# Revit family: Haworth_Enclose_Wall_Solid_Special
name_source: partatom
category: Furniture Systems
revit_build: Autodesk Revit 2018 (Build: 20170223_1515(x64)
units: mm (PartAtom-declared; Revit-internal decimal feet)

## family parameters
Always vertical = Yes
Cut with Voids When Loaded = No
OmniClass Number = 23.25.40.14
OmniClass Title = Demountable Partitions
Part Type = Normal
Room Calculation Point = No
Round Connector Dimension = Use Diameter
Shared = Yes
Work Plane-Based = No

## types (1)
- 36" x 40"
    # of Panels Back = 1
    # of Panels Front = 1
    Actual # of Panels Back = 1
    Actual # of Panels Front = 1
    Actual Height = 40 "
    Actual Panel 1 Back Height = 32 "
    Actual Panel 1 Front Height = 32 "
    Actual Panel 2 Back Height = 32 "
    Actual Panel 2 Front Height = 32 "
    Actual Width = 36 "
    Assembly Code = C1010200
    Base Height = 1.25 "
    Cap Height = 1 "
    Ceiling Mount = Yes
    Description = Wall Solid - Special
    End of Run Finish = Haworth _ Polymer _ Black
    End of Run Width = 0.155 "
    Frame Depth = 4 "
    Frame Finish = Haworth _ Metal _ Brushed Aluminum
    Glass Offset = 4.75 "
    Height = 40 "
    Horizontal Bottom Adjuster Width = 3.875 "
    Horizontal Bottom Trim Width = 2.5 "
    Horizontal Frame Width = 0.875 "
    Horizontal Top Adjuster Width = 2.625 "
    Horizontal Top Trim Width = 1.5 "
    Manufacturer = Haworth
    Material Options = http://surfaces.haworth.com
    Max # of Panels = 3
    Max. Height = 144 "
    Max. Width = 60 "
    Min. Height = 24 "
    Min. Width = 8 "
    Min/Max Height = 84-144 in.
    Min/Max Width = 8-60 in.
    Model = Haworth - Enclose
    Offset Back = 9.84 "
    Offset Front = 9.84 "
    Panel 1 Back Height = 32 "
    Panel 1 Front Height = 32 "
    Panel 2 Back Height = 64 "
    Panel 2 Front Height = 64 "
    Panel Depth = 0.5 "
    Panel Height Back = 29.16 "
    Panel Height Front = 29.16 "
    Panel Height Note = All Heights are A.F.F.
    Panel Size Note = 8in increments
    Panel Width = 35.69 "
    Raceway Finish = Haworth _ Metal _ Brushed Aluminum
    Raceway Panel Back = Yes
    Raceway Panel Back Height = 8.59 "
    Raceway Panel Front = Yes
    Raceway Panel Front Height = 8.59 "
    Raceway Panel Width = 35.69 "
    Revision Number = 4
    Size = Verify Final Dim. w/ Haworth
    Sustainability Info = http://www.haworth.com
    URL = www.haworth.com
    URL - Product = http://www.haworth.com
    Vertical Frame Width = 0.875 "
    Warranty = http://www.haworth.com
    Width = 36 "

## geometry (parser evidence)
native form markers: Sweep x11
no freeform markers — native parametric forms only
